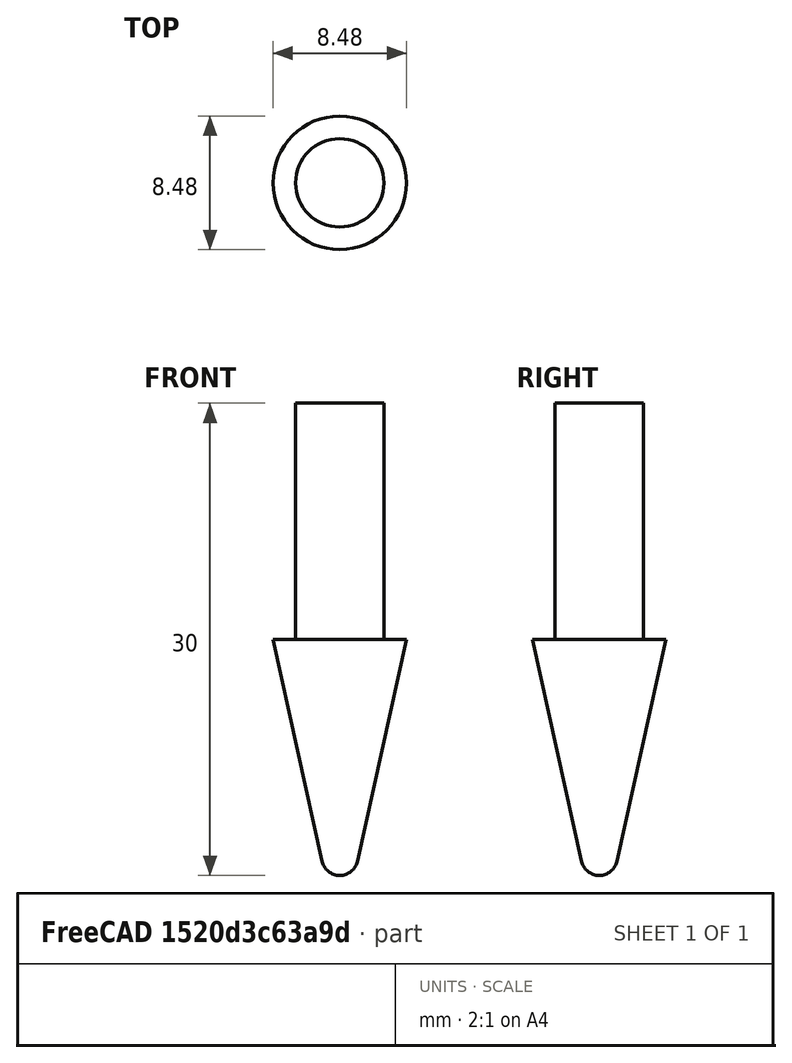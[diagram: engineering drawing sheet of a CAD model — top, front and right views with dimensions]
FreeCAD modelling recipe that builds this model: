
FCSTD DOCUMENT  (FreeCAD 0.18R16093 (Git))
Label: Punta_Palo
License: All rights reserved
LicenseURL: http://en.wikipedia.org/wiki/All_rights_reserved
objects: Sketcher::SketchObject×1, PartDesign::Revolution×1, PartDesign::Body×1
note: 4 computed .brp shape members not serialized (recipe doc carries the construction recipe); baked Part::Feature solids carry a one-line shape summary decoded from their .brp

FEATURE [Sketcher::SketchObject] Sketch128
  MapMode = 5
  Placement = pos=(0,0,0) rot=(1,0,0;1.5708rad)
  Support = -> [XZ_Plane032]
  sketch-geometry (6):
    g0: LineSegment StartX=0 StartY=0 StartZ=0 EndX=-2.8 EndY=0 EndZ=0
    g1: LineSegment StartX=-2.8 StartY=0 StartZ=0 EndX=-2.8 EndY=-15 EndZ=0
    g2: LineSegment StartX=-2.8 StartY=-15 StartZ=0 EndX=-4.24 EndY=-15 EndZ=0
    g3: LineSegment StartX=0 StartY=-30 StartZ=0 EndX=0 EndY=0 EndZ=0
    g4: ArcOfCircle CenterX=0 CenterY=-28.85 CenterZ=0 NormalX=0 NormalY=0 NormalZ=1 AngleXU=0 Radius=1.15 StartAngle=3.35919 EndAngle=4.71239
    g5: LineSegment StartX=-4.24 StartY=-15 StartZ=0 EndX=-1.12288 EndY=-29.0983 EndZ=0
  constraints (17):
    c: Coincident(g0,g1)
    c: Coincident(g1,g2)
    c: Coincident(g3,g0)
    c: Vertical(g3)
    c: Horizontal(g0)
    c: Vertical(g1)
    c: Horizontal(g2)
    c: PointOnObject(g4,g3)
    c: Coincident(g3,g4)
    c: Distance(g0) = 2.8
    c: Distance(g2) = 1.44
    c: DistanceY(g3,g2) = 15
    c: Tangent(g4,g5) = -1.5708
    c: Coincident(g5,g2)
    c: Radius(g4) = 1.15
    c: Coincident(g0,g-1)
    c: DistanceY(g3,g3) = 30
FEATURE [PartDesign::Revolution] Revolution005
  Angle = 360
  Axis = (0,2e-16,1)
  Base = (0,0,0)
  Placement = pos=(0,0,0) rot=(1,0,0;1.5708rad)
  Profile = -> Sketch128
  ReferenceAxis = -> Sketch128 [V_Axis]
FEATURE [PartDesign::Body] Body032  label="Punta"
  Group = -> [Sketch128,Revolution005]
  Origin = -> Origin032
  Placement = pos=(0,0,-65) rot=(0,0,1;0rad)
  Tip = -> Revolution005
